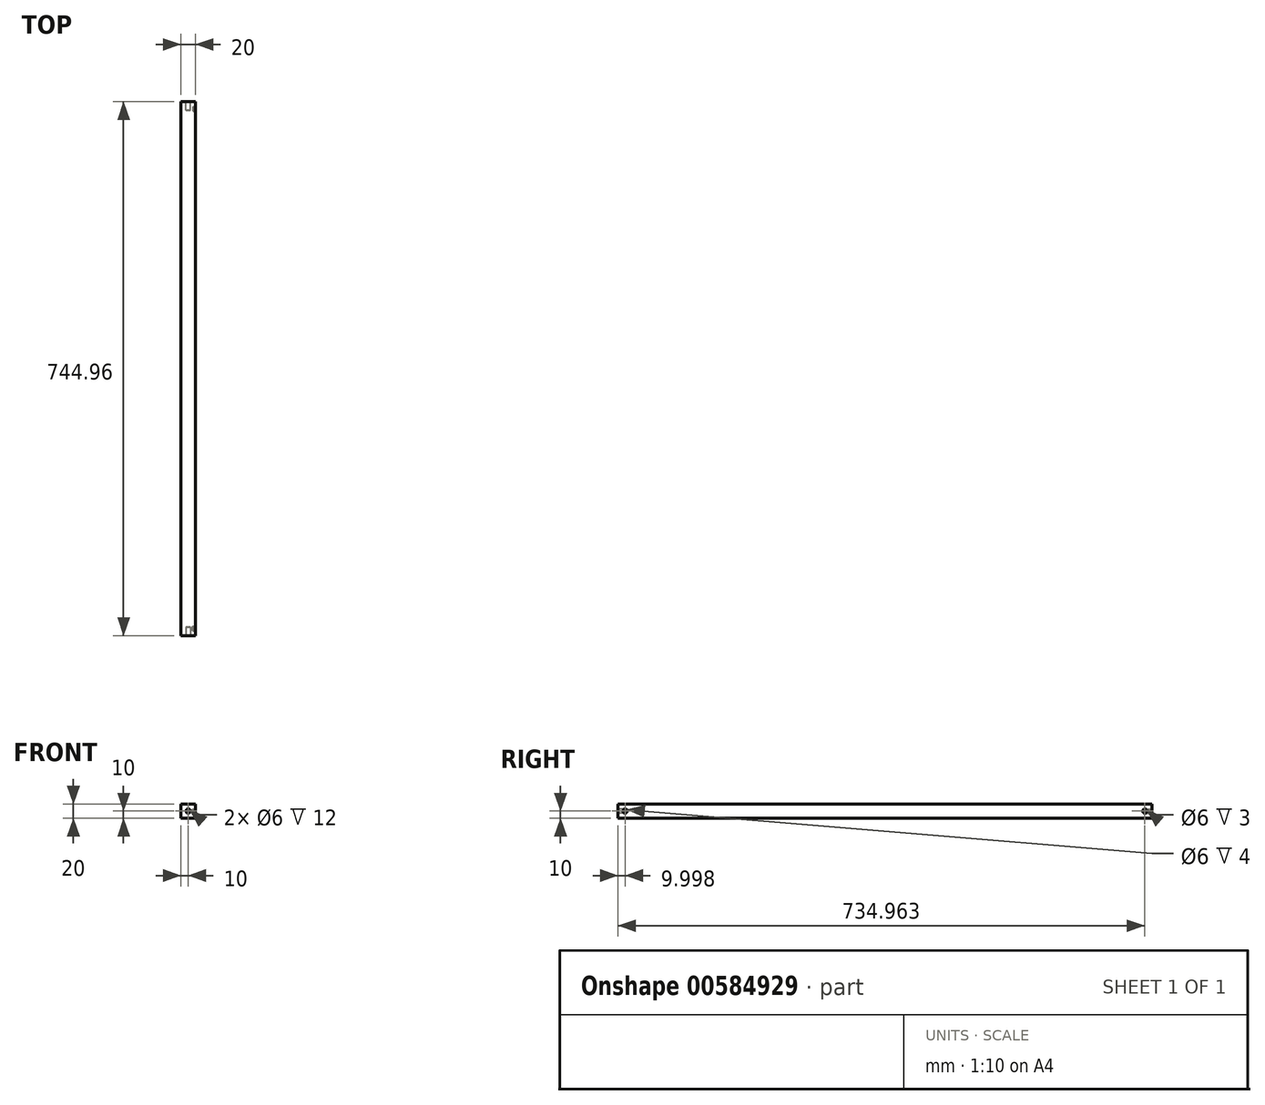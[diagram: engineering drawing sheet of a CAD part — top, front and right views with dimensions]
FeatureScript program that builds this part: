
annotation { "Feature Type Name" : "Feature", "Feature Type Description" : "" }
export const myFeature = defineFeature(function(context is Context, id is Id, definition is map)
    precondition{}
    {
        {
            var Q0;
            Q0=qCreatedBy(makeId("Front.planeOp"),FACE);
            var sketch = newSketch(context, id + "F0", { "sketchPlane" : qUnion([Q0])});
            skLineSegment(sketch, "E0.bottom", {"start": v(0, 0) * mm, "end": v(20, 0) * mm});
            skLineSegment(sketch, "E0.top", {"start": v(0, 20) * mm, "end": v(20, 20) * mm});
            skLineSegment(sketch, "E0.left", {"start": v(0, 0) * mm, "end": v(0, 20) * mm});
            skLineSegment(sketch, "E0.right", {"start": v(20, 0) * mm, "end": v(20, 20) * mm});
            skSolve(sketch);
        }
        {
            var Q0;
            Q0=makeQuery(id+"F0.imprint","IMPRINT",FACE,{"disambiguationData":[TD([[makeQuery(id+"F0.imprint","IMPRINT",EDGE,{"derivedFrom":sQuery(id+"F0.wireOp",EDGE,"E0.bottom")}),1.0]])]});
            extrude(context, id + "F1", {"entities" : qUnion([Q0]), "depth" : 744.97 * mm, "offsetDistance" : 25 * mm, "symmetric" : true});
        }
        {
            var Q0;
            Q0=makeQuery(id+"F1.opExtrude","CAP_FACE",FACE,{"disambiguationData":[OSD([sQuery(id+"F0.wireOp",EDGE,"E0.bottom"),sQuery(id+"F0.wireOp",EDGE,"E0.top"),sQuery(id+"F0.wireOp",EDGE,"E0.left"),sQuery(id+"F0.wireOp",EDGE,"E0.right")])],"isStart":false});
            var sketch = newSketch(context, id + "F2", { "sketchPlane" : qUnion([Q0])});
            skCircle(sketch, "E1", {"center": v(10, 10) * mm, "radius": 3 * mm});
            skPoint(sketch, "E1.centerSnap0", {"position": v(10, 20) * mm});
            skSolve(sketch);
        }
        {
            var Q0;
            Q0=makeQuery(id+"F2.imprint","IMPRINT",FACE,{"disambiguationData":[TD([[makeQuery(id+"F2.imprint","IMPRINT",EDGE,{"derivedFrom":sQuery(id+"F2.wireOp",EDGE,"E1")}),1.0]])]});
            extrude(context, id + "F3", {"entities" : qUnion([Q0]), "operationType" : NewBodyOperationType.REMOVE, "oppositeDirection" : true, "depth" : 12 * mm, "offsetDistance" : 25 * mm});
        }
        {
            var Q0;
            Q0=makeQuery(id+"F1.opExtrude","CAP_FACE",FACE,{"disambiguationData":[OSD([sQuery(id+"F0.wireOp",EDGE,"E0.bottom"),sQuery(id+"F0.wireOp",EDGE,"E0.top"),sQuery(id+"F0.wireOp",EDGE,"E0.left"),sQuery(id+"F0.wireOp",EDGE,"E0.right")])],"isStart":true});
            var sketch = newSketch(context, id + "F4", { "sketchPlane" : qUnion([Q0])});
            skCircle(sketch, "E2", {"center": v(-10, 10) * mm, "radius": 3 * mm});
            skSolve(sketch);
        }
        {
            var Q0;
            Q0=makeQuery(id+"F4.imprint","IMPRINT",FACE,{"disambiguationData":[TD([[makeQuery(id+"F4.imprint","IMPRINT",EDGE,{"derivedFrom":sQuery(id+"F4.wireOp",EDGE,"E2")}),1.0]])]});
            extrude(context, id + "F5", {"entities" : qUnion([Q0]), "operationType" : NewBodyOperationType.REMOVE, "oppositeDirection" : true, "depth" : 12 * mm, "offsetDistance" : 25 * mm});
        }
        {
            var Q0;
            Q0=makeQuery(id+"F1.opExtrude","SWEPT_FACE",FACE,{"disambiguationData":[OSD([sQuery(id+"F0.wireOp",EDGE,"E0.right")])]});
            var sketch = newSketch(context, id + "F6", { "sketchPlane" : qUnion([Q0])});
            skCircle(sketch, "E3", {"center": v(362.48, 10) * mm, "radius": 3 * mm});
            skSolve(sketch);
        }
        {
            var Q0;
            Q0=makeQuery(id+"F6.imprint","IMPRINT",FACE,{"disambiguationData":[TD([[makeQuery(id+"F6.imprint","IMPRINT",EDGE,{"derivedFrom":sQuery(id+"F6.wireOp",EDGE,"E3")}),1.0]])]});
            extrude(context, id + "F7", {"entities" : qUnion([Q0]), "operationType" : NewBodyOperationType.REMOVE, "oppositeDirection" : true, "depth" : 3 * mm, "offsetDistance" : 25 * mm});
        }
        {
            var Q0;
            Q0=makeQuery(id+"F1.opExtrude","SWEPT_FACE",FACE,{"disambiguationData":[OSD([sQuery(id+"F0.wireOp",EDGE,"E0.right")])]});
            var sketch = newSketch(context, id + "F8", { "sketchPlane" : qUnion([Q0])});
            skCircle(sketch, "E4", {"center": v(-362.48, 10) * mm, "radius": 3 * mm});
            skSolve(sketch);
        }
        {
            var Q0;
            Q0=makeQuery(id+"F8.imprint","IMPRINT",FACE,{"disambiguationData":[TD([[makeQuery(id+"F8.imprint","IMPRINT",EDGE,{"derivedFrom":sQuery(id+"F8.wireOp",EDGE,"E4")}),1.0]])]});
            extrude(context, id + "F9", {"entities" : qUnion([Q0]), "operationType" : NewBodyOperationType.REMOVE, "oppositeDirection" : true, "depth" : 4 * mm, "offsetDistance" : 25 * mm});
        }
    });
